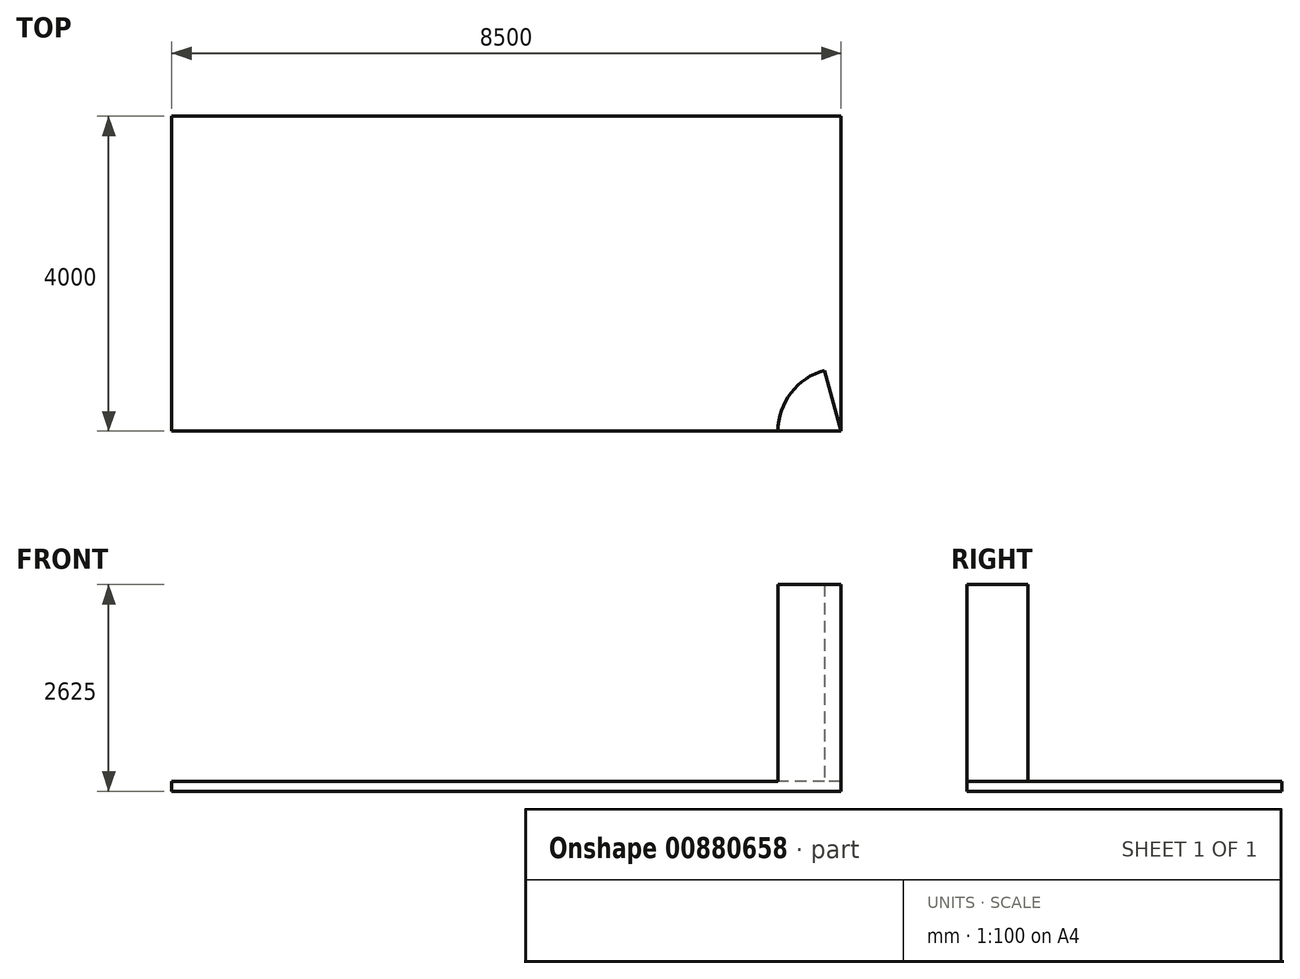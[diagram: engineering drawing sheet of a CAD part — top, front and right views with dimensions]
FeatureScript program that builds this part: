
annotation { "Feature Type Name" : "Feature", "Feature Type Description" : "" }
export const myFeature = defineFeature(function(context is Context, id is Id, definition is map)
    precondition{}
    {
        {
            var Q0;
            Q0=qCreatedBy(makeId("Top.planeOp"),FACE);
            var sketch = newSketch(context, id + "F0", { "sketchPlane" : qUnion([Q0])});
            skLineSegment(sketch, "E0.bottom", {"start": v(4250, 2000) * mm, "end": v(-4250, 2000) * mm});
            skLineSegment(sketch, "E0.top", {"start": v(4250, -2000) * mm, "end": v(-4250, -2000) * mm});
            skLineSegment(sketch, "E0.left", {"start": v(4250, 2000) * mm, "end": v(4250, -2000) * mm});
            skLineSegment(sketch, "E0.right", {"start": v(-4250, 2000) * mm, "end": v(-4250, -2000) * mm});
            skPoint(sketch, "E0.middle", {"position": v(0, 0) * mm});
            skSolve(sketch);
        }
        {
            var Q0;
            Q0 = qSketchRegion(id + "F0", true);
            extrude(context, id + "F1", {"entities" : qUnion([Q0]), "depth" : 100 * mm, "offsetDistance" : 25 * mm});
        }
        {
            var Q0;
            Q0=makeQuery(id+"F1.opExtrude","CAP_FACE",FACE,{"disambiguationData":[OSD([sQuery(id+"F0.wireOp",EDGE,"E0.bottom"),sQuery(id+"F0.wireOp",EDGE,"E0.top"),sQuery(id+"F0.wireOp",EDGE,"E0.left"),sQuery(id+"F0.wireOp",EDGE,"E0.right")])],"isStart":false});
            extrude(context, id + "F2", {"entities" : qUnion([Q0]), "operationType" : NewBodyOperationType.ADD, "depth" : 25 * mm, "offsetDistance" : 25 * mm});
        }
        {
            var Q0;
            Q0=makeQuery(id+"F2.opExtrude","CAP_FACE",FACE,{"disambiguationData":[OSD([sQuery(id+"F0.wireOp",EDGE,"E0.bottom"),sQuery(id+"F0.wireOp",EDGE,"E0.top"),sQuery(id+"F0.wireOp",EDGE,"E0.left"),sQuery(id+"F0.wireOp",EDGE,"E0.right")])],"isStart":false});
            var sketch = newSketch(context, id + "F3", { "sketchPlane" : qUnion([Q0])});
            skLineSegment(sketch, "E1", {"start": v(4250, -2000) * mm, "end": v(4042.94, -1227.26) * mm});
            skLineSegment(sketch, "E2", {"start": v(4250, -2000) * mm, "end": v(3450, -2000) * mm});
            skArc(sketch, "E3", {"start": v(4042.94, -1227.26) * mm, "mid": v(3615.32, -1513) * mm, "end": v(3450, -2000) * mm});
            skSolve(sketch);
        }
        {
            var Q0;
            Q0=makeQuery(id+"F3.imprint","IMPRINT",FACE,{"disambiguationData":[TD([[makeQuery(id+"F3.imprint","IMPRINT",EDGE,{"derivedFrom":sQuery(id+"F3.wireOp",EDGE,"E1")}),1.0]])]});
            extrude(context, id + "F4", {"entities" : qUnion([Q0]), "operationType" : NewBodyOperationType.ADD, "depth" : 2500 * mm, "offsetDistance" : 25 * mm});
        }
    });
